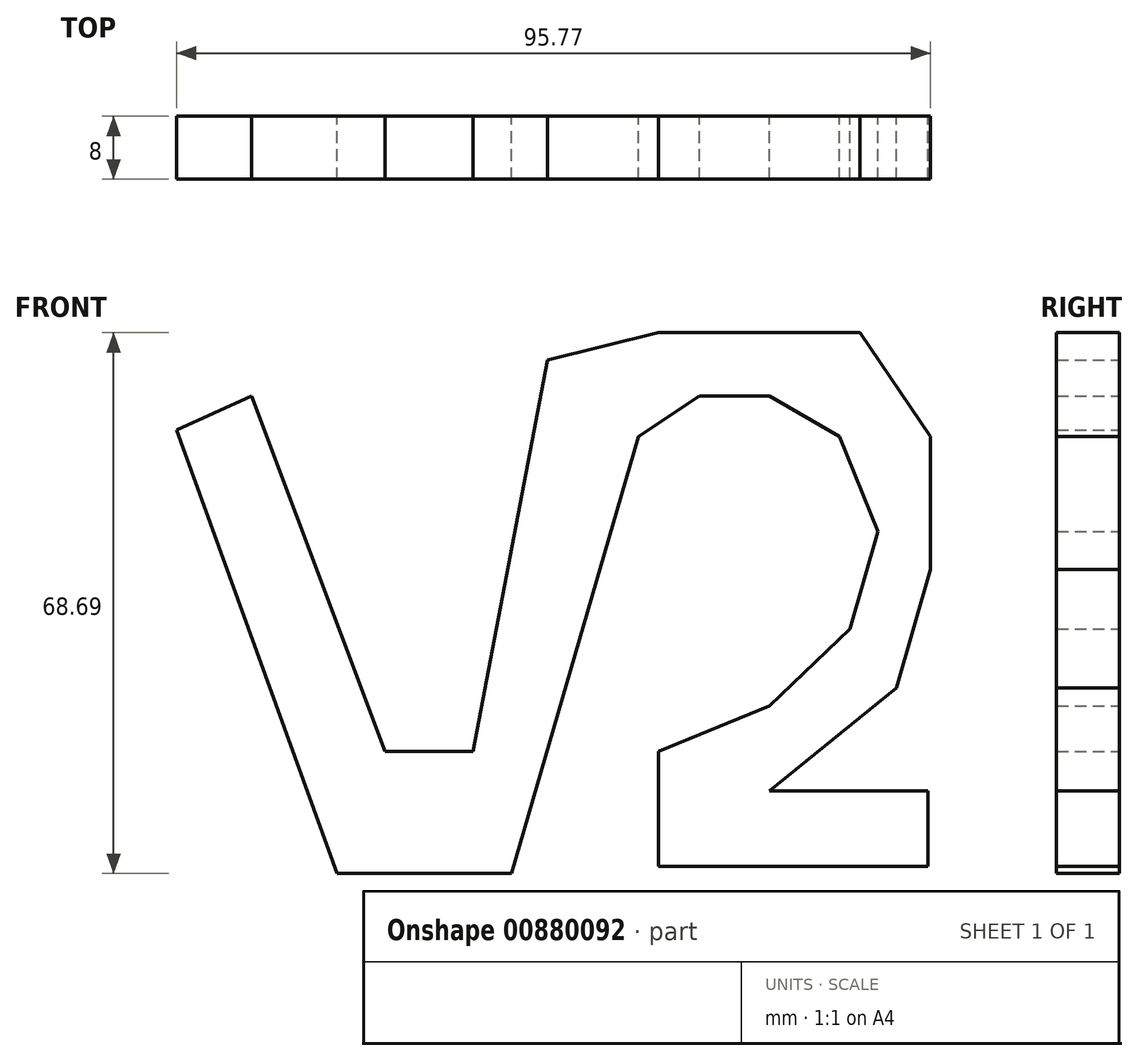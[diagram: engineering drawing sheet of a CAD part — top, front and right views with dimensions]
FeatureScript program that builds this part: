
annotation { "Feature Type Name" : "Feature", "Feature Type Description" : "" }
export const myFeature = defineFeature(function(context is Context, id is Id, definition is map)
    precondition{}
    {
        {
            var Q0;
            Q0=qCreatedBy(makeId("Front.planeOp"),FACE);
            var sketch = newSketch(context, id + "F0", { "sketchPlane" : qUnion([Q0])});
            skLineSegment(sketch, "E0", {"start": v(-69.4, 45.84) * mm, "end": v(-49, -10.5) * mm});
            skLineSegment(sketch, "E1", {"start": v(-49, -10.5) * mm, "end": v(-26.87, -10.5) * mm});
            skLineSegment(sketch, "E2", {"start": v(-26.87, -10.5) * mm, "end": v(-10.78, 44.98) * mm});
            skLineSegment(sketch, "E3", {"start": v(-10.78, 44.98) * mm, "end": v(-3.02, 50.15) * mm});
            skLineSegment(sketch, "E4", {"start": v(-3.02, 50.15) * mm, "end": v(5.9, 50.15) * mm});
            skLineSegment(sketch, "E5", {"start": v(5.9, 50.15) * mm, "end": v(14.8, 44.98) * mm});
            skLineSegment(sketch, "E6", {"start": v(14.8, 44.98) * mm, "end": v(19.69, 32.9) * mm});
            skLineSegment(sketch, "E7", {"start": v(19.69, 32.9) * mm, "end": v(16.1, 20.58) * mm});
            skLineSegment(sketch, "E8", {"start": v(16.1, 20.58) * mm, "end": v(5.9, 10.78) * mm});
            skLineSegment(sketch, "E9", {"start": v(5.9, 10.78) * mm, "end": v(-8.2, 5.03) * mm});
            skLineSegment(sketch, "E10", {"start": v(-8.2, 5.03) * mm, "end": v(-8.2, -9.63) * mm});
            skLineSegment(sketch, "E11", {"start": v(-8.2, -9.63) * mm, "end": v(26.01, -9.63) * mm});
            skLineSegment(sketch, "E12", {"start": v(26.01, -9.63) * mm, "end": v(26.01, 0) * mm});
            skLineSegment(sketch, "E13", {"start": v(26.01, 0) * mm, "end": v(5.9, 0) * mm});
            skLineSegment(sketch, "E14", {"start": v(5.9, 0) * mm, "end": v(21.99, 13.08) * mm});
            skLineSegment(sketch, "E15", {"start": v(21.99, 13.08) * mm, "end": v(26.36, 28.14) * mm});
            skLineSegment(sketch, "E16", {"start": v(26.36, 28.14) * mm, "end": v(26.36, 44.98) * mm});
            skLineSegment(sketch, "E17", {"start": v(26.36, 44.98) * mm, "end": v(17.39, 58.2) * mm});
            skLineSegment(sketch, "E18", {"start": v(17.39, 58.2) * mm, "end": v(-8.2, 58.2) * mm});
            skLineSegment(sketch, "E19", {"start": v(-8.2, 58.2) * mm, "end": v(-22.27, 54.75) * mm});
            skLineSegment(sketch, "E20", {"start": v(-22.27, 54.75) * mm, "end": v(-31.76, 5.03) * mm});
            skLineSegment(sketch, "E21", {"start": v(-31.76, 5.03) * mm, "end": v(-42.97, 5.03) * mm});
            skLineSegment(sketch, "E22", {"start": v(-42.97, 5.03) * mm, "end": v(-59.92, 50.15) * mm});
            skLineSegment(sketch, "E23", {"start": v(-59.92, 50.15) * mm, "end": v(-69.4, 45.84) * mm});
            skSolve(sketch);
        }
        {
            var Q0;
            Q0=makeQuery(id+"F0.imprint","IMPRINT",FACE,{"disambiguationData":[TD([[makeQuery(id+"F0.imprint","IMPRINT",EDGE,{"derivedFrom":sQuery(id+"F0.wireOp",EDGE,"E0")}),1.0]])]});
            extrude(context, id + "F1", {"entities" : qUnion([Q0]), "depth" : 8 * mm, "offsetDistance" : 25 * mm});
        }
    });
